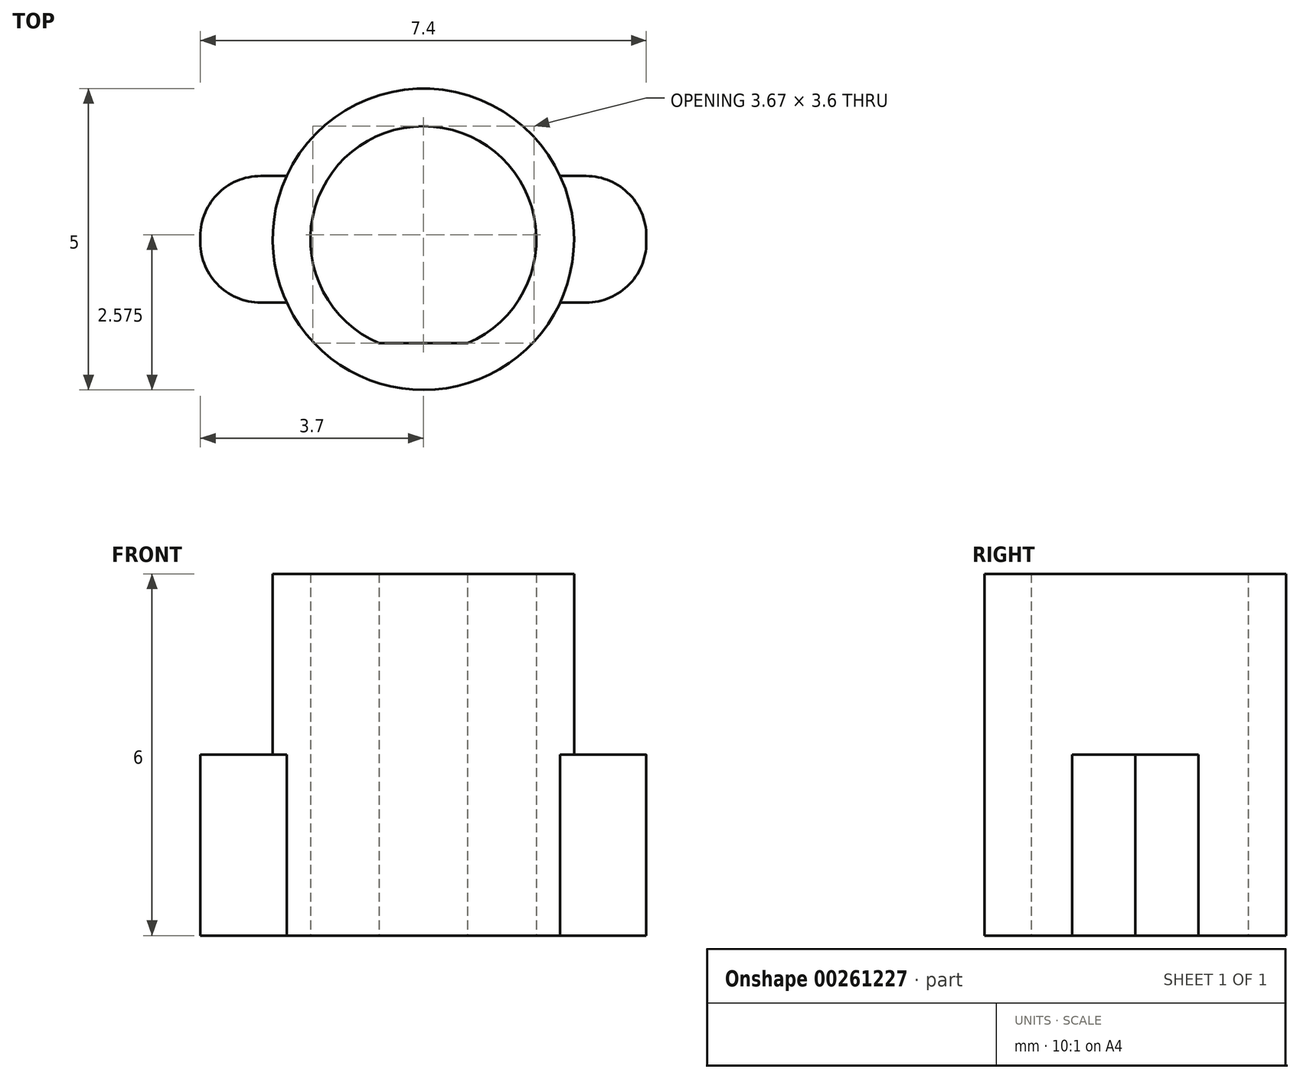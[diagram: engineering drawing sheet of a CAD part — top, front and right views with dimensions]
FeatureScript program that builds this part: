
annotation { "Feature Type Name" : "Feature", "Feature Type Description" : "" }
export const myFeature = defineFeature(function(context is Context, id is Id, definition is map)
    precondition{}
    {
        {
            var Q0;
            Q0=qCreatedBy(makeId("Top.planeOp"),FACE);
            var sketch = newSketch(context, id + "F0", { "sketchPlane" : qUnion([Q0])});
            skCircle(sketch, "E0", {"center": v(0, 0) * mm, "radius": 2.5 * mm});
            skArc(sketch, "E1.0", {"start": v(0.73, -1.72) * mm, "mid": v(0, 1.88) * mm, "end": v(-0.73, -1.72) * mm});
            skCircle(sketch, "E2.0", {"center": v(0, 0) * mm, "radius": 3.7 * mm, "construction": true});
            skLineSegment(sketch, "E3", {"start": v(0, 0) * mm, "end": v(0, 4.6) * mm, "construction": true});
            skLineSegment(sketch, "E4", {"start": v(0, 0) * mm, "end": v(-1.43, 0) * mm, "construction": true});
            skLineSegment(sketch, "E5", {"start": v(3.7, 0.05) * mm, "end": v(3.7, -0.05) * mm});
            skLineSegment(sketch, "E6", {"start": v(2.27, 1.05) * mm, "end": v(2.7, 1.05) * mm});
            skArc(sketch, "E7", {"start": v(3.7, 0) * mm, "mid": v(3.42, 0.74) * mm, "end": v(2.7, 1.05) * mm});
            skArc(sketch, "E8.MirrorC", {"start": v(3.7, 0) * mm, "mid": v(3.42, -0.74) * mm, "end": v(2.7, -1.05) * mm});
            skArc(sketch, "E9.MirrorC", {"start": v(-2.03, 1.46) * mm, "mid": v(2.16, -1.26) * mm, "end": v(-2.27, 1.05) * mm});
            skLineSegment(sketch, "E10", {"start": v(2.7, -1.05) * mm, "end": v(2.27, -1.05) * mm});
            skArc(sketch, "E11.MirrorCS", {"start": v(-3.7, 0) * mm, "mid": v(-3.42, -0.74) * mm, "end": v(-2.7, -1.05) * mm});
            skArc(sketch, "E12.MirrorCS", {"start": v(-3.7, 0) * mm, "mid": v(-3.42, 0.74) * mm, "end": v(-2.7, 1.05) * mm});
            skLineSegment(sketch, "E13", {"start": v(-2.7, 1.05) * mm, "end": v(-2.27, 1.05) * mm});
            skLineSegment(sketch, "E14", {"start": v(-2.7, -1.05) * mm, "end": v(-2.27, -1.05) * mm});
            skLineSegment(sketch, "E15", {"start": v(-0.73, -1.73) * mm, "end": v(0.73, -1.72) * mm});
            skPoint(sketch, "E16.MirrorCS.start.orphan", {"position": v(2.03, -1.46) * mm});
            skPoint(sketch, "E17.start.orphan", {"position": v(2.03, 1.46) * mm});
            skSolve(sketch);
        }
        {
            var Q0;
            Q0=makeQuery(id+"F0.imprint","IMPRINT",FACE,{"disambiguationData":[TD([[makeQuery(id+"F0.imprint","IMPRINT",EDGE,{"derivedFrom":sQuery(id+"F0.wireOp",EDGE,"E1.0")}),-1.0]])]});
            extrude(context, id + "F1", {"entities" : qUnion([Q0]), "depth" : 6 * mm});
        }
        {
            var Q0;
            {var subQ5=sQuery(id+"F0.wireOp",EDGE,"E6");Q0=makeQuery(id+"F0.imprint","IMPRINT",FACE,{"disambiguationData":[TD([[makeQuery(id+"F0.imprint","IMPRINT",EDGE,{"derivedFrom":subQ5}),-1.0]])]});}
            var Q1;
            Q1=makeQuery(id+"F0.imprint","IMPRINT",FACE,{"disambiguationData":[TD([[makeQuery(id+"F0.imprint","IMPRINT",EDGE,{"derivedFrom":sQuery(id+"F0.wireOp",EDGE,"E11.MirrorCS")}),1.0]])]});
            extrude(context, id + "F2", {"entities" : qUnion([Q0, Q1]), "operationType" : NewBodyOperationType.ADD, "depth" : 3 * mm});
        }
    });
